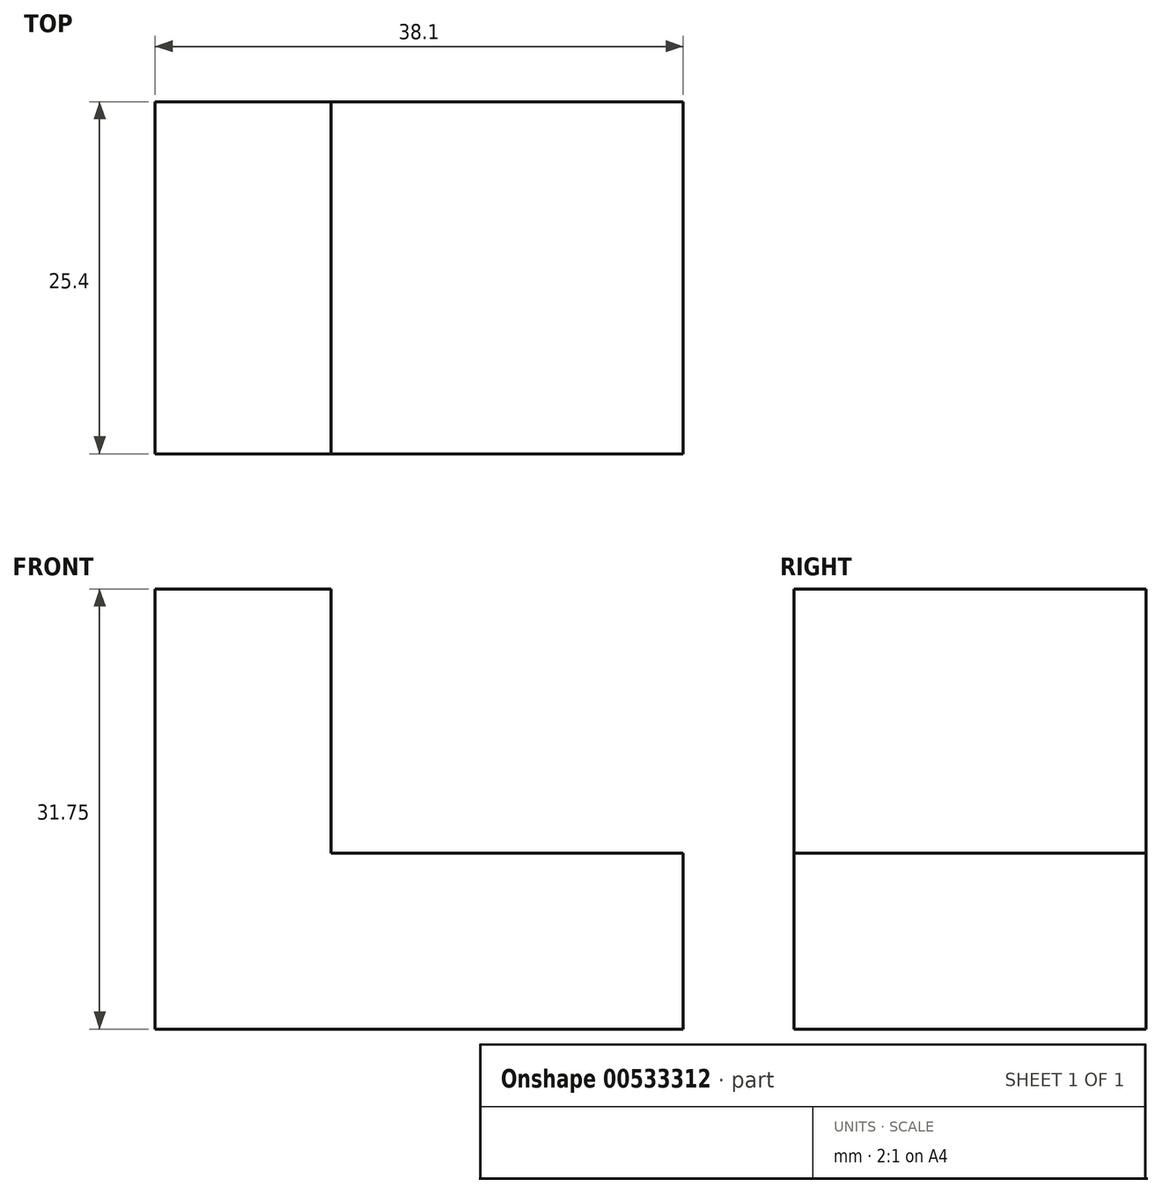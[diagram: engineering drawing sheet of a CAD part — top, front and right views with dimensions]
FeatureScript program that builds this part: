
annotation { "Feature Type Name" : "Feature", "Feature Type Description" : "" }
export const myFeature = defineFeature(function(context is Context, id is Id, definition is map)
    precondition{}
    {
        {
            var Q0;
            Q0=qCreatedBy(makeId("Front.planeOp"),FACE);
            var sketch = newSketch(context, id + "F0", { "sketchPlane" : qUnion([Q0])});
            skLineSegment(sketch, "E0", {"start": v(0, 31.75) * mm, "end": v(12.7, 31.75) * mm});
            skLineSegment(sketch, "E1", {"start": v(0, 0) * mm, "end": v(0, 31.75) * mm});
            skLineSegment(sketch, "E2", {"start": v(0, 0) * mm, "end": v(38.1, 0) * mm});
            skLineSegment(sketch, "E3", {"start": v(12.7, 31.75) * mm, "end": v(12.7, 12.7) * mm});
            skLineSegment(sketch, "E4", {"start": v(12.7, 12.7) * mm, "end": v(38.1, 12.7) * mm});
            skLineSegment(sketch, "E5", {"start": v(38.1, 12.7) * mm, "end": v(38.1, 0) * mm});
            skSolve(sketch);
        }
        {
            var Q0;
            Q0 = qSketchRegion(id + "F0", true);
            extrude(context, id + "F1", {"entities" : qUnion([Q0]), "depth" : 25.4 * mm, "offsetDistance" : 25.4 * mm});
        }
    });
